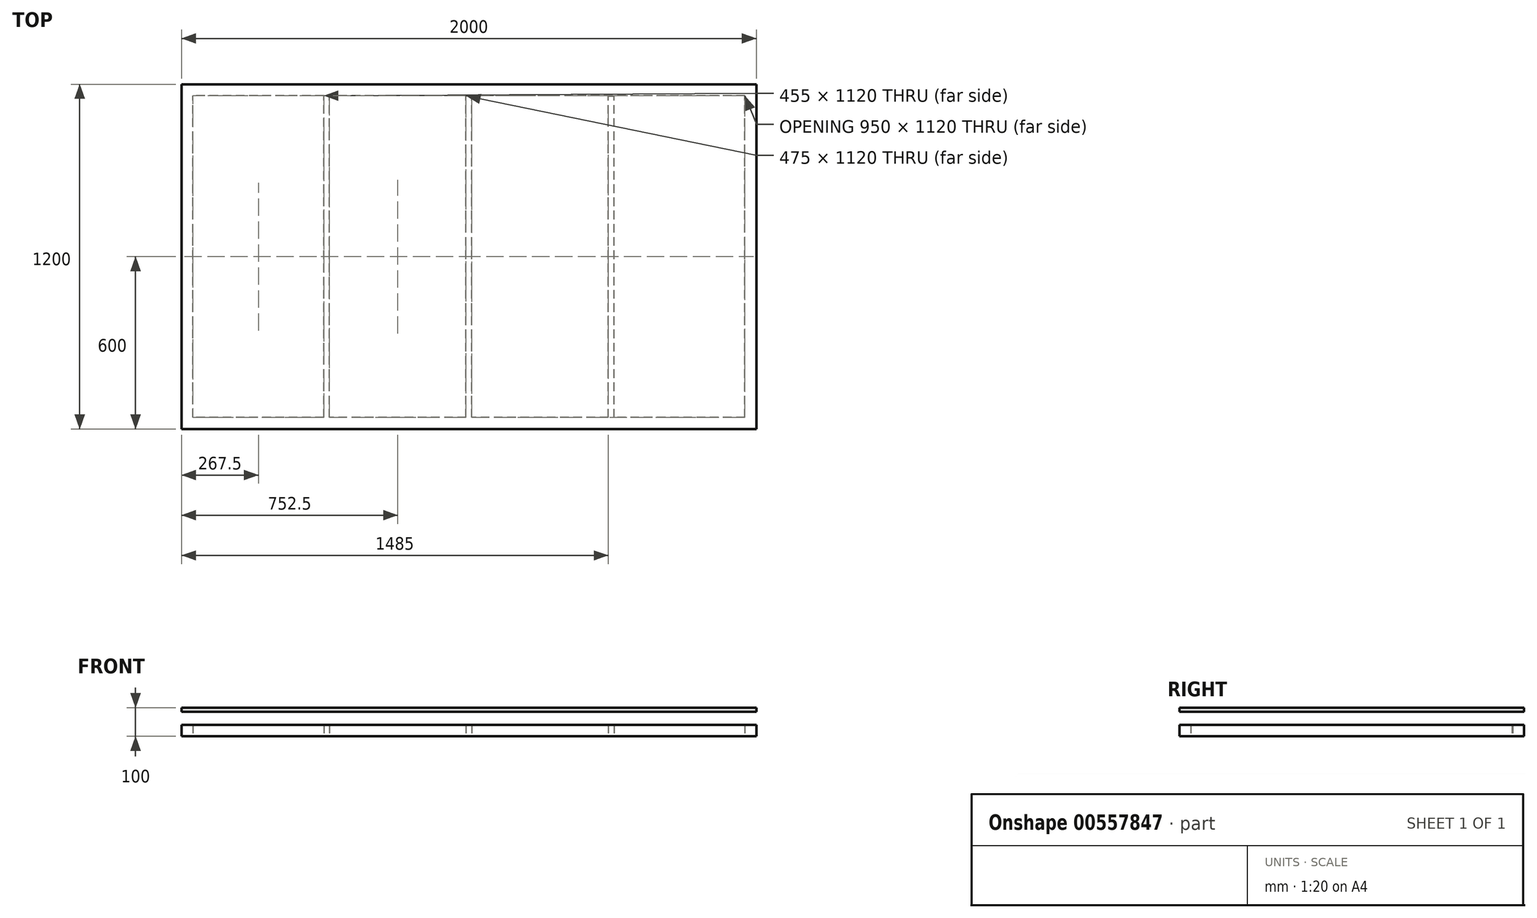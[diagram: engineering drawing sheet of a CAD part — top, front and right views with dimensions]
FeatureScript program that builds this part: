
annotation { "Feature Type Name" : "Feature", "Feature Type Description" : "" }
export const myFeature = defineFeature(function(context is Context, id is Id, definition is map)
    precondition{}
    {
        {
            var Q0;
            Q0=qCreatedBy(makeId("Top.planeOp"),FACE);
            var sketch = newSketch(context, id + "F0", { "sketchPlane" : qUnion([Q0])});
            skLineSegment(sketch, "E0.bottom", {"start": v(1000, -600) * mm, "end": v(-1000, -600) * mm});
            skLineSegment(sketch, "E0.top", {"start": v(1000, 600) * mm, "end": v(-1000, 600) * mm});
            skLineSegment(sketch, "E0.left", {"start": v(1000, -600) * mm, "end": v(1000, 600) * mm});
            skLineSegment(sketch, "E0.right", {"start": v(-1000, -600) * mm, "end": v(-1000, 600) * mm});
            skPoint(sketch, "E0.middle", {"position": v(0, 0) * mm});
            skLineSegment(sketch, "E1.0", {"start": v(960, 560) * mm, "end": v(-960, 560) * mm});
            skLineSegment(sketch, "E1.1", {"start": v(960, -560) * mm, "end": v(960, 560) * mm});
            skLineSegment(sketch, "E1.2", {"start": v(960, -560) * mm, "end": v(-960, -560) * mm});
            skLineSegment(sketch, "E1.3", {"start": v(-960, -560) * mm, "end": v(-960, 560) * mm});
            skSolve(sketch);
        }
        {
            var Q0;
            Q0=qCreatedBy(makeId("Top.planeOp"),FACE);
            var sketch = newSketch(context, id + "F1", { "sketchPlane" : qUnion([Q0])});
            skLineSegment(sketch, "E2.bottom", {"start": v(10, -560) * mm, "end": v(-10, -560) * mm});
            skLineSegment(sketch, "E2.top", {"start": v(10, 560) * mm, "end": v(-10, 560) * mm});
            skLineSegment(sketch, "E2.left", {"start": v(10, -560) * mm, "end": v(10, 560) * mm});
            skLineSegment(sketch, "E2.right", {"start": v(-10, -560) * mm, "end": v(-10, 560) * mm});
            skPoint(sketch, "E2.middle", {"position": v(0, 0) * mm});
            skLineSegment(sketch, "E3.1.0.0", {"start": v(505, -561.95) * mm, "end": v(505, 558.05) * mm});
            skLineSegment(sketch, "E3.1.0.1", {"start": v(485, -561.95) * mm, "end": v(485, 558.05) * mm});
            skPoint(sketch, "E3.1.0.2", {"position": v(495, -1.95) * mm});
            skLineSegment(sketch, "E3.1.0.3", {"start": v(505, -561.95) * mm, "end": v(485, -561.95) * mm});
            skLineSegment(sketch, "E3.1.0.4", {"start": v(505, 558.05) * mm, "end": v(485, 558.05) * mm});
            skLineSegment(sketch, "E3.direction1", {"start": v(-10, -560) * mm, "end": v(485, -561.95) * mm, "construction": true});
            skLineSegment(sketch, "E4.1.0.0", {"start": v(-505, -560) * mm, "end": v(-505, 560) * mm});
            skLineSegment(sketch, "E4.1.0.1", {"start": v(-485, -560) * mm, "end": v(-485, 560) * mm});
            skPoint(sketch, "E4.1.0.2", {"position": v(-495, 0) * mm});
            skLineSegment(sketch, "E4.1.0.3", {"start": v(-485, 560) * mm, "end": v(-505, 560) * mm});
            skLineSegment(sketch, "E4.1.0.4", {"start": v(-485, -560) * mm, "end": v(-505, -560) * mm});
            skLineSegment(sketch, "E4.direction1", {"start": v(-10, -560) * mm, "end": v(-505, -560) * mm, "construction": true});
            skSolve(sketch);
        }
        {
            var Q0;
            Q0 = qSketchRegion(id + "F0", true);
            extrude(context, id + "F2", {"entities" : qUnion([Q0]), "depth" : 40 * mm, "offsetDistance" : 25 * mm});
        }
        {
            var Q0;
            Q0 = qSketchRegion(id + "F1", true);
            extrude(context, id + "F3", {"entities" : qUnion([Q0]), "operationType" : NewBodyOperationType.ADD, "depth" : 40 * mm, "offsetDistance" : 25 * mm});
        }
        {
            var Q0;
            Q0=qCreatedBy(makeId("Top.planeOp"),FACE);
            cPlane(context, id + "F4", {"entities" : qUnion([Q0]), "cplaneType" : CPlaneType.OFFSET, "offset" : 100 * mm, "width" : 150 * mm, "height" : 150 * mm});
        }
        {
            var Q0;
            Q0=qCreatedBy(id+"F4.planeOp",FACE);
            var sketch = newSketch(context, id + "F5", { "sketchPlane" : qUnion([Q0])});
            skLineSegment(sketch, "E5.bottom", {"start": v(1000, -600) * mm, "end": v(-1000, -600) * mm});
            skLineSegment(sketch, "E5.top", {"start": v(1000, 600) * mm, "end": v(-1000, 600) * mm});
            skLineSegment(sketch, "E5.left", {"start": v(1000, -600) * mm, "end": v(1000, 600) * mm});
            skLineSegment(sketch, "E5.right", {"start": v(-1000, -600) * mm, "end": v(-1000, 600) * mm});
            skPoint(sketch, "E5.middle", {"position": v(0, 0) * mm});
            skSolve(sketch);
        }
        {
            var Q0;
            Q0 = qSketchRegion(id + "F5", true);
            extrude(context, id + "F6", {"entities" : qUnion([Q0]), "operationType" : NewBodyOperationType.ADD, "oppositeDirection" : true, "depth" : 15 * mm, "offsetDistance" : 25 * mm});
        }
    });
